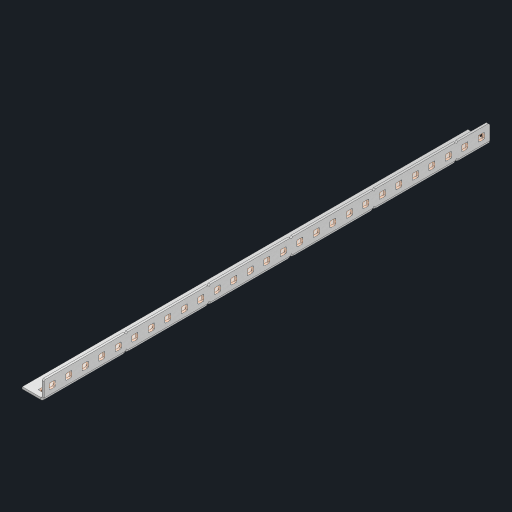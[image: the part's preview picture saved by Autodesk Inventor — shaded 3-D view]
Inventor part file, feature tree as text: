
AUTODESK INVENTOR PART (.ipt)
format: ipt  version: 2023 (Build 270158000, 158)  size: 903,168 bytes
history: native  units: in
note: dims shown in document units (in); Inventor stores cm internally (conversion verified against a paired STEP export)
features: other x59, extrude x53, sheet_metal_op x10, sketch x8, mirror x1, pattern_linear x1, chamfer x1
ambient origin geometry x8: Origin, YZ Plane, XZ Plane, XY Plane, X Axis, Y Axis, Z Axis, Center Point
bodies: Solid1 (feature_tree), Body (feature_tree)
feature tree (133):
  other  "Flange Pattern Plane"
  sheet_metal_op  "Flange Pattern"
  sheet_metal_op  "Body Pattern"
  other  "Arc Length"
  mirror  "Notch Mirror"
  pattern_linear  "Notch Pattern"  Spacing1=0.25in  [1 undecoded]
  chamfer  "End Chamfer"
  extrude  "Half Cut"  Depth=0.0625in
  sketch  "Sketch1"  dims[d0=1.5in]
  other  "Plate1"
  sketch  "Sketch2"  dims[d1=13.5in]
  other  "Plate2"
  sheet_metal_op  "Bend1"
  sheet_metal_op  "Corner1"
  sketch  "Sketch3"  dims[d2=0.0625in]
  other  "Flange Pattern Sketch"
  sketch  "Sketch7"  dims[d3=0.0625in]
  other  "Srf1"
  other  "Srf2"
  sketch  "Sketch8"  dims[d4=0.0312in]
  sketch  "Sketch9"  dims[d5=0.125in]
  other  "Srf91"
  sheet_metal_op  "Body Pattern Sketch"
  other  "Srf92"
  sketch  "Sketch13"  dims[d6=0.0625in]
  sketch  "Sketch14"  dims[d7=0.5in d8=90.0deg d9=0.0312in d10=0.25in d11=0.0625in d12=0.0625in d16=0.182in d17=0.02in d18=0.0625in d19=0.0in d20=0.25in d21=0.25in d46=0.172in d47=1.0in d48=0.0in d49=0.182in d50=0.02in d51=0.25in d52=0.25in d53=0.0625in d54=0.0in d55=0.172in d56=1.0in d57=0.0in d60=10.6299in d62=0.5in d63=0.3937in d65=0.5in d85=0.1473in d86=0.1782in d88=0.04in d89=0.0625in d90=0.0in d91=0.04in d92=0.0491in d95=2.5in d96=0.04in d97=0.25in d98=45.0deg d101=0.0in d102=2.497in d131=0.5in d132=10.6299in d134=0.5in d139=0.5in]
  other  "Srf856"
  other  "Srf1310"
  other  "Srf1311"
  other  "Srf1312"
  other  "Srf1376"
  other  "Srf1377"
  other  "Srf1728"
  other  "Srf1755"
  other  "Srf1878"
  other  "Srf1879"
  other  "Srf1880"
  other  "Srf1881"
  other  "Srf1882"
  other  "Srf1883"
  other  "Srf1884"
  other  "Srf1885"
  other  "Srf1886"
  other  "Srf1887"
  other  "Srf1888"
  other  "Srf1889"
  other  "Srf1890"
  other  "Srf1891"
  other  "Srf1892"
  other  "Srf1893"
  other  "Srf1894"
  other  "Srf1895"
  other  "Srf1896"
  other  "Srf1897"
  other  "Srf1898"
  other  "Srf1942"
  other  "Srf1943"
  other  "Srf1944"
  other  "Srf1945"
  other  "Srf1946"
  other  "Srf1947"
  other  "Srf1948"
  other  "Srf1949"
  other  "Srf1950"
  other  "Srf1951"
  other  "Srf1952"
  other  "Srf1953"
  other  "Srf1954"
  other  "Srf1955"
  other  "Srf1956"
  other  "Srf1957"
  other  "Srf1958"
  other  "Srf1959"
  other  "Srf1960"
  other  "Srf1961"
  other  "Srf1962"
  sheet_metal_op  "Flange Stamp"
  sheet_metal_op  "Flange Circle"
  sheet_metal_op  "Body Stamp"
  sheet_metal_op  "Body Circle"
  sheet_metal_op  "Notch"
  extrude  "ExtrusionSrf2"  Depth=0.0625in
  extrude  "ExtrusionSrf92"  Depth=0.5in
  extrude  "ExtrusionSrf856"  Depth=0.02in
  extrude  "ExtrusionSrf1310"  Depth=0.0625in
  extrude  "ExtrusionSrf1311"  TaperAngle=0.0deg  [1 undecoded]
  extrude  "ExtrusionSrf1312"  Depth=0.5in
  extrude  "ExtrusionSrf1376"  Depth=0.5in
  extrude  "ExtrusionSrf1377"  Depth=0.5in
  extrude  "ExtrusionSrf1728"  Depth=0.5in TaperAngle=0.0deg
  extrude  "ExtrusionSrf1755"  Depth=0.5in
  extrude  "ExtrusionSrf1878"  Depth=0.02in
  extrude  "ExtrusionSrf1879"  Depth=0.5in
  extrude  "ExtrusionSrf1880"  Depth=0.5in
  extrude  "ExtrusionSrf1881"  Depth=0.0625in
  extrude  "ExtrusionSrf1882"  TaperAngle=0.0deg  [1 undecoded]
  extrude  "ExtrusionSrf1883"  Depth=0.5in
  extrude  "ExtrusionSrf1884"  Depth=0.5in TaperAngle=0.0deg
  extrude  "ExtrusionSrf1885"  Depth=0.5in
  extrude  "ExtrusionSrf1886"  Depth=0.5in
  extrude  "ExtrusionSrf1887"  Depth=0.5in
  extrude  "ExtrusionSrf1888"  Depth=0.5in
  extrude  "ExtrusionSrf1889"  Depth=0.5in
  extrude  "ExtrusionSrf1890"  Depth=0.0625in
  extrude  "ExtrusionSrf1891"  TaperAngle=0.0deg  [1 undecoded]
  extrude  "ExtrusionSrf1892"  Depth=0.5in
  extrude  "ExtrusionSrf1893"  Depth=0.5in
  extrude  "ExtrusionSrf1894"  Depth=0.5in
  extrude  "ExtrusionSrf1895"  Depth=0.5in TaperAngle=45.0deg
  extrude  "ExtrusionSrf1896"  TaperAngle=0.0deg  [1 undecoded]
  extrude  "ExtrusionSrf1897"  Depth=0.5in
  extrude  "ExtrusionSrf1898"  Depth=0.5in
  extrude  "ExtrusionSrf1942"  Depth=0.5in
  extrude  "ExtrusionSrf1943"  Depth=0.5in
  extrude  "ExtrusionSrf1944"  Depth=0.5in
  extrude  "ExtrusionSrf1945"  [1 undecoded]
  extrude  "ExtrusionSrf1946"  [1 undecoded]
  extrude  "ExtrusionSrf1947"  [1 undecoded]
  extrude  "ExtrusionSrf1948"  [1 undecoded]
  extrude  "ExtrusionSrf1949"  [1 undecoded]
  extrude  "ExtrusionSrf1950"  [1 undecoded]
  extrude  "ExtrusionSrf1951"  [1 undecoded]
  extrude  "ExtrusionSrf1952"  [1 undecoded]
  extrude  "ExtrusionSrf1953"  [1 undecoded]
  extrude  "ExtrusionSrf1954"  [1 undecoded]
  extrude  "ExtrusionSrf1955"  [1 undecoded]
  extrude  "ExtrusionSrf1956"  [1 undecoded]
  extrude  "ExtrusionSrf1957"  [1 undecoded]
  extrude  "ExtrusionSrf1958"  [1 undecoded]
  extrude  "ExtrusionSrf1959"  [1 undecoded]
  extrude  "ExtrusionSrf1960"  [1 undecoded]
  extrude  "ExtrusionSrf1961"  [1 undecoded]
  extrude  "ExtrusionSrf1962"  [1 undecoded]
note: 23 required parameter values undecoded (feature->parameter linkage not recoverable at this tier; creation-order binding heuristic only, values carry confidence <= 0.55)
